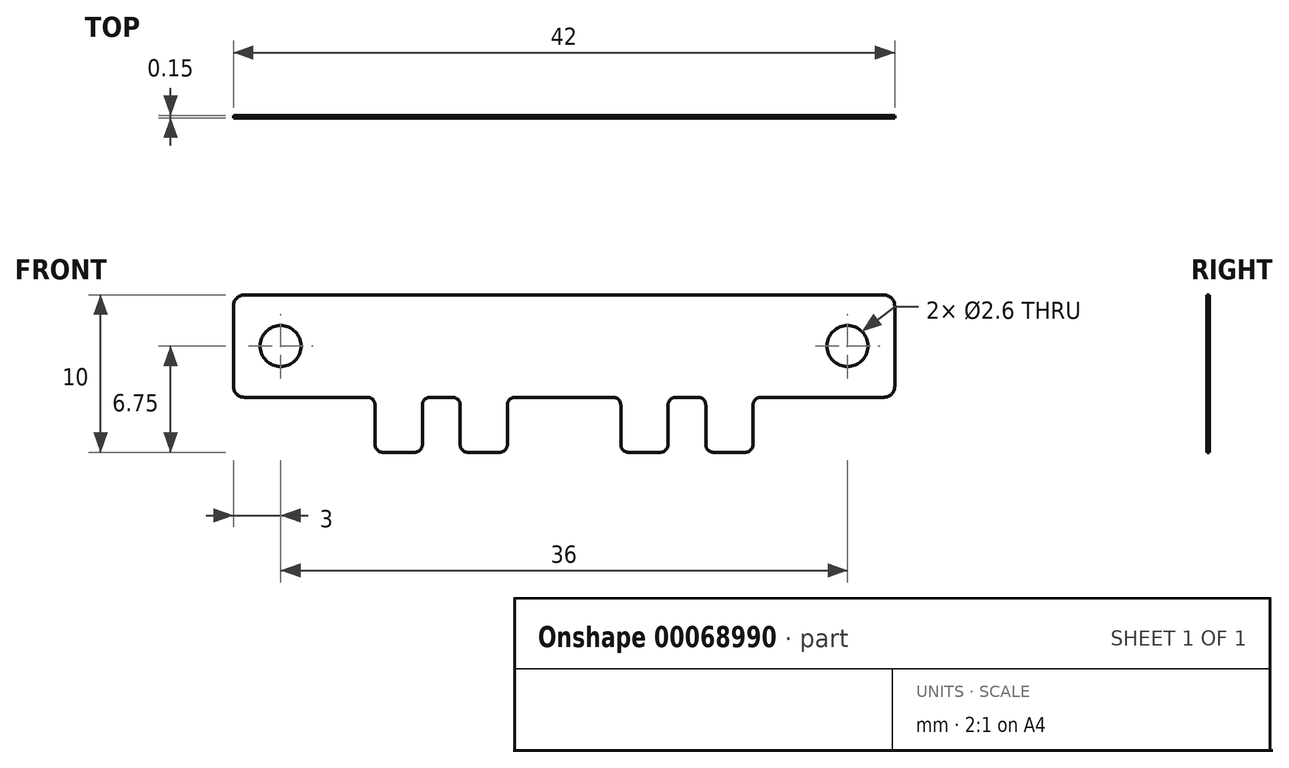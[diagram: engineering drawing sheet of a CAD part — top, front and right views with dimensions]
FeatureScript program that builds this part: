
annotation { "Feature Type Name" : "Feature", "Feature Type Description" : "" }
export const myFeature = defineFeature(function(context is Context, id is Id, definition is map)
    precondition{}
    {
        {
            var Q0;
            Q0=qCreatedBy(makeId("Front.planeOp"),FACE);
            var sketch = newSketch(context, id + "F0", { "sketchPlane" : qUnion([Q0])});
            skLineSegment(sketch, "E0.bottom", {"start": v(0, 0) * mm, "end": v(3, 0) * mm});
            skLineSegment(sketch, "E0.top", {"start": v(0, 6.5) * mm, "end": v(31, 6.5) * mm});
            skLineSegment(sketch, "E0.left", {"start": v(0, 0) * mm, "end": v(0, 6.5) * mm, "construction": true});
            skLineSegment(sketch, "E0.right", {"start": v(31, 0) * mm, "end": v(31, 6.5) * mm, "construction": true});
            skLineSegment(sketch, "E1", {"start": v(0, 0) * mm, "end": v(-4.8, 0) * mm});
            skLineSegment(sketch, "E2", {"start": v(-5.5, 0.7) * mm, "end": v(-5.5, 5.8) * mm});
            skLineSegment(sketch, "E3", {"start": v(-4.8, 6.5) * mm, "end": v(0, 6.5) * mm});
            skLineSegment(sketch, "E4", {"start": v(15.5, 6.5) * mm, "end": v(15.5, 0) * mm, "construction": true});
            skLineSegment(sketch, "E5.MirrorCS", {"start": v(31, 0) * mm, "end": v(35.8, 0) * mm});
            skLineSegment(sketch, "E6.MirrorCS", {"start": v(36.5, 0.7) * mm, "end": v(36.5, 5.8) * mm});
            skLineSegment(sketch, "E7.MirrorCS", {"start": v(35.8, 6.5) * mm, "end": v(31, 6.5) * mm});
            skPoint(sketch, "E8.centerSnap1", {"position": v(-5.5, 3.25) * mm});
            skLineSegment(sketch, "E9.top", {"start": v(4, -3.5) * mm, "end": v(6, -3.5) * mm});
            skLineSegment(sketch, "E9.left", {"start": v(3.5, -0.5) * mm, "end": v(3.5, -3) * mm});
            skLineSegment(sketch, "E9.right", {"start": v(6.5, -0.5) * mm, "end": v(6.5, -3) * mm});
            skLineSegment(sketch, "E10", {"start": v(7.7, 0) * mm, "end": v(7.7, 6.5) * mm, "construction": true});
            skPoint(sketch, "E11.visualSharp", {"position": v(6.5, -3.5) * mm});
            skArc(sketch, "E11.filletArc", {"start": v(6, -3.5) * mm, "mid": v(6.35, -3.35) * mm, "end": v(6.5, -3) * mm});
            skPoint(sketch, "E12.visualSharp", {"position": v(3.5, -3.5) * mm});
            skArc(sketch, "E12.filletArc", {"start": v(3.5, -3) * mm, "mid": v(3.65, -3.35) * mm, "end": v(4, -3.5) * mm});
            skLineSegment(sketch, "E13.trimOffspring", {"start": v(7, 0) * mm, "end": v(8.4, 0) * mm});
            skPoint(sketch, "E14.visualSharp", {"position": v(6.5, 0) * mm});
            skArc(sketch, "E14.filletArc", {"start": v(7, 0) * mm, "mid": v(6.65, -0.15) * mm, "end": v(6.5, -0.5) * mm});
            skPoint(sketch, "E15.visualSharp", {"position": v(3.5, 0) * mm});
            skArc(sketch, "E15.filletArc", {"start": v(3.5, -0.5) * mm, "mid": v(3.35, -0.15) * mm, "end": v(3, 0) * mm});
            skArc(sketch, "E16.MirrorCS", {"start": v(11.9, -3) * mm, "mid": v(11.75, -3.35) * mm, "end": v(11.4, -3.5) * mm});
            skArc(sketch, "E17.MirrorCS", {"start": v(8.4, 0) * mm, "mid": v(8.75, -0.15) * mm, "end": v(8.9, -0.5) * mm});
            skArc(sketch, "E18.MirrorCS", {"start": v(9.4, -3.5) * mm, "mid": v(9.05, -3.35) * mm, "end": v(8.9, -3) * mm});
            skArc(sketch, "E19.MirrorCS", {"start": v(11.9, -0.5) * mm, "mid": v(12.05, -0.15) * mm, "end": v(12.4, 0) * mm});
            skPoint(sketch, "E20.MirrorP", {"position": v(11.9, -3.5) * mm});
            skLineSegment(sketch, "E21.MirrorCS", {"start": v(11.4, -3.5) * mm, "end": v(9.4, -3.5) * mm});
            skLineSegment(sketch, "E22.MirrorCS", {"start": v(8.9, -0.5) * mm, "end": v(8.9, -3) * mm});
            skLineSegment(sketch, "E23.MirrorCS", {"start": v(11.9, -0.5) * mm, "end": v(11.9, -3) * mm});
            skPoint(sketch, "E24.MirrorP", {"position": v(8.9, -3.5) * mm});
            skPoint(sketch, "E25.MirrorP", {"position": v(11.9, 0) * mm});
            skPoint(sketch, "E26.MirrorP", {"position": v(8.9, 0) * mm});
            skArc(sketch, "E27.MirrorCS", {"start": v(25, -3.5) * mm, "mid": v(24.65, -3.35) * mm, "end": v(24.5, -3) * mm});
            skArc(sketch, "E28.MirrorCS", {"start": v(24, 0) * mm, "mid": v(24.35, -0.15) * mm, "end": v(24.5, -0.5) * mm});
            skArc(sketch, "E29.MirrorCS", {"start": v(21.6, -3.5) * mm, "mid": v(21.95, -3.35) * mm, "end": v(22.1, -3) * mm});
            skArc(sketch, "E30.MirrorCS", {"start": v(22.6, 0) * mm, "mid": v(22.25, -0.15) * mm, "end": v(22.1, -0.5) * mm});
            skArc(sketch, "E31.MirrorCS", {"start": v(19.1, -0.5) * mm, "mid": v(18.95, -0.15) * mm, "end": v(18.6, 0) * mm});
            skArc(sketch, "E32.MirrorCS", {"start": v(19.1, -3) * mm, "mid": v(19.25, -3.35) * mm, "end": v(19.6, -3.5) * mm});
            skArc(sketch, "E33.MirrorCS", {"start": v(27.5, -3) * mm, "mid": v(27.35, -3.35) * mm, "end": v(27, -3.5) * mm});
            skArc(sketch, "E34.MirrorCS", {"start": v(27.5, -0.5) * mm, "mid": v(27.65, -0.15) * mm, "end": v(28, 0) * mm});
            skPoint(sketch, "E35.MirrorP", {"position": v(19.1, 0) * mm});
            skLineSegment(sketch, "E36.MirrorCS", {"start": v(24.5, -0.5) * mm, "end": v(24.5, -3) * mm});
            skLineSegment(sketch, "E37.MirrorCS", {"start": v(19.6, -3.5) * mm, "end": v(21.6, -3.5) * mm});
            skLineSegment(sketch, "E38.MirrorCS", {"start": v(19.1, -0.5) * mm, "end": v(19.1, -3) * mm});
            skPoint(sketch, "E39.MirrorP", {"position": v(19.1, -3.5) * mm});
            skPoint(sketch, "E40.MirrorP", {"position": v(27.5, -3.5) * mm});
            skPoint(sketch, "E41.MirrorP", {"position": v(22.1, -3.5) * mm});
            skPoint(sketch, "E42.MirrorP", {"position": v(27.5, 0) * mm});
            skPoint(sketch, "E43.MirrorP", {"position": v(24.5, -3.5) * mm});
            skPoint(sketch, "E44.MirrorP", {"position": v(22.1, 0) * mm});
            skLineSegment(sketch, "E45.MirrorCS", {"start": v(27.5, -0.5) * mm, "end": v(27.5, -3) * mm});
            skLineSegment(sketch, "E46.MirrorCS", {"start": v(22.1, -0.5) * mm, "end": v(22.1, -3) * mm});
            skPoint(sketch, "E47.MirrorP", {"position": v(24.5, 0) * mm});
            skLineSegment(sketch, "E48.MirrorCS", {"start": v(27, -3.5) * mm, "end": v(25, -3.5) * mm});
            skLineSegment(sketch, "E49.trimOffspring", {"start": v(22.6, 0) * mm, "end": v(24, 0) * mm});
            skLineSegment(sketch, "E50.trimOffspring", {"start": v(28, 0) * mm, "end": v(31, 0) * mm});
            skLineSegment(sketch, "E51.trimOffspring", {"start": v(12.4, 0) * mm, "end": v(18.6, 0) * mm});
            skCircle(sketch, "E52", {"center": v(-2.5, 3.25) * mm, "radius": 1.3 * mm});
            skCircle(sketch, "E53.MirrorC", {"center": v(33.5, 3.25) * mm, "radius": 1.3 * mm});
            skPoint(sketch, "E54.visualSharp", {"position": v(-5.5, 6.5) * mm});
            skArc(sketch, "E54.filletArc", {"start": v(-4.8, 6.5) * mm, "mid": v(-5.3, 6.3) * mm, "end": v(-5.5, 5.8) * mm});
            skPoint(sketch, "E55.visualSharp", {"position": v(-5.5, 0) * mm});
            skArc(sketch, "E55.filletArc", {"start": v(-5.5, 0.7) * mm, "mid": v(-5.3, 0.2) * mm, "end": v(-4.8, 0) * mm});
            skPoint(sketch, "E56.visualSharp", {"position": v(36.5, 6.5) * mm});
            skArc(sketch, "E56.filletArc", {"start": v(36.5, 5.8) * mm, "mid": v(36.3, 6.3) * mm, "end": v(35.8, 6.5) * mm});
            skPoint(sketch, "E57.visualSharp", {"position": v(36.5, 0) * mm});
            skArc(sketch, "E57.filletArc", {"start": v(35.8, 0) * mm, "mid": v(36.3, 0.2) * mm, "end": v(36.5, 0.7) * mm});
            skSolve(sketch);
        }
        {
            var Q0;
            Q0 = qSketchRegion(id + "F0", true);
            extrude(context, id + "F1", {"entities" : qUnion([Q0]), "depth" : 0.15 * mm});
        }
    });
